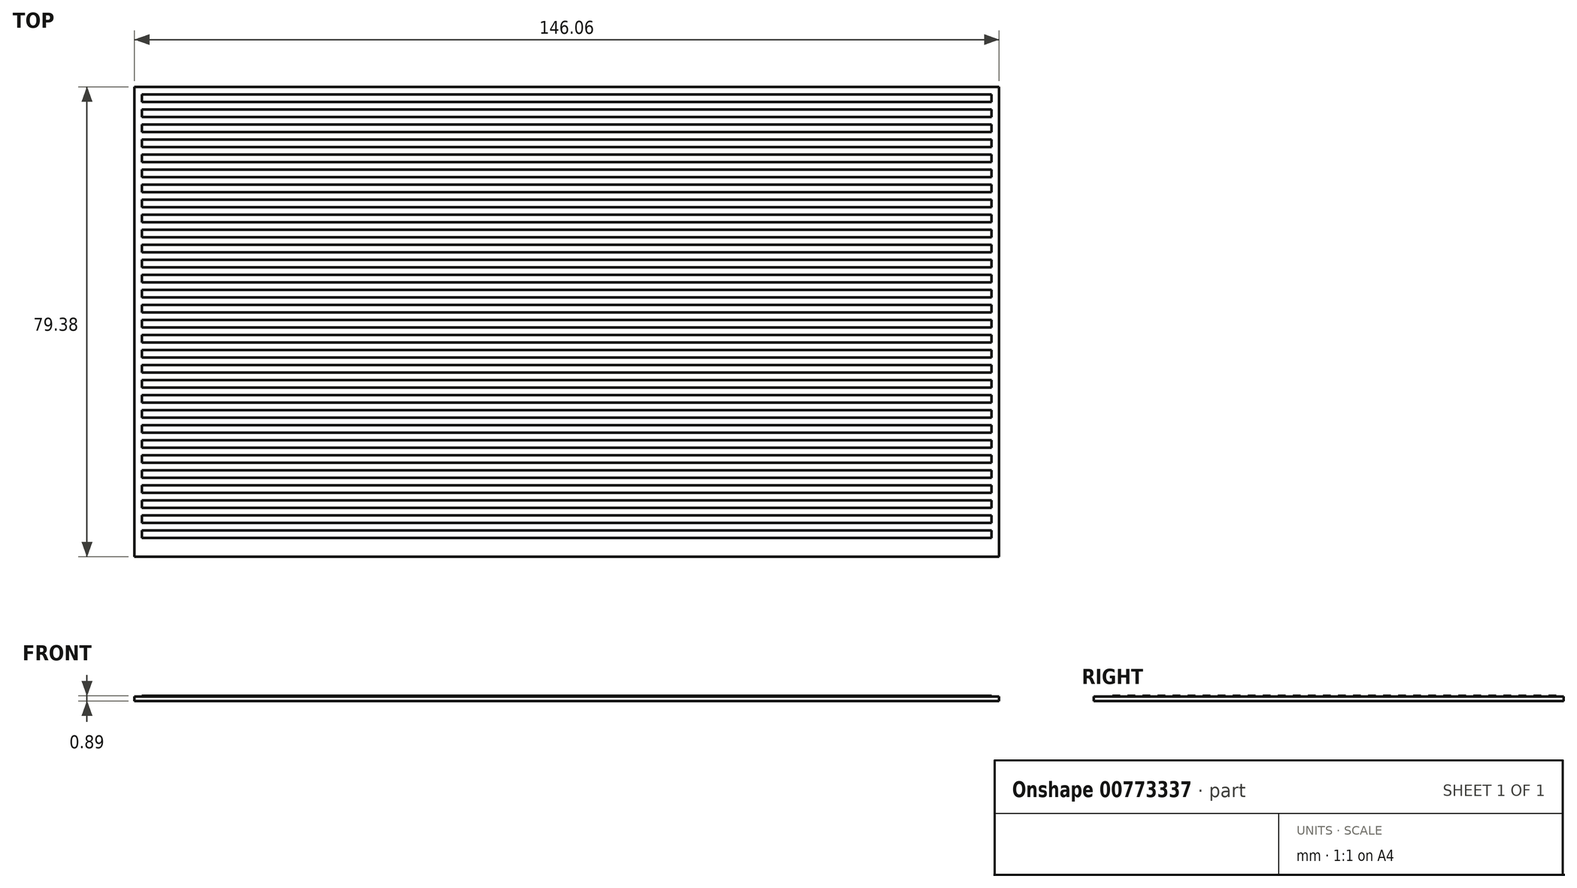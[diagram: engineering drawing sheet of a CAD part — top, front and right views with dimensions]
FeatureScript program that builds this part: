
annotation { "Feature Type Name" : "Feature", "Feature Type Description" : "" }
export const myFeature = defineFeature(function(context is Context, id is Id, definition is map)
    precondition{}
    {
        {
            var Q0;
            Q0=qCreatedBy(makeId("Top.planeOp"),FACE);
            var sketch = newSketch(context, id + "F0", { "sketchPlane" : qUnion([Q0])});
            skLineSegment(sketch, "E0.bottom", {"start": v(73.03, 39.69) * mm, "end": v(-73.03, 39.69) * mm});
            skLineSegment(sketch, "E0.top", {"start": v(73.03, -39.69) * mm, "end": v(-73.03, -39.69) * mm});
            skLineSegment(sketch, "E0.left", {"start": v(73.03, 39.69) * mm, "end": v(73.03, -39.69) * mm});
            skLineSegment(sketch, "E0.right", {"start": v(-73.03, 39.69) * mm, "end": v(-73.03, -39.69) * mm});
            skPoint(sketch, "E0.middle", {"position": v(0, 0) * mm});
            skSolve(sketch);
        }
        {
            var Q0;
            Q0 = qSketchRegion(id + "F0", true);
            extrude(context, id + "F1", {"entities" : qUnion([Q0]), "depth" : 0.76 * mm, "offsetDistance" : 25.4 * mm});
        }
        {
            var Q0;
            Q0=makeQuery(id+"F1.opExtrude","CAP_FACE",FACE,{"disambiguationData":[OSD([sQuery(id+"F0.wireOp",EDGE,"E0.bottom"),sQuery(id+"F0.wireOp",EDGE,"E0.top"),sQuery(id+"F0.wireOp",EDGE,"E0.left"),sQuery(id+"F0.wireOp",EDGE,"E0.right")])],"isStart":false});
            var sketch = newSketch(context, id + "F2", { "sketchPlane" : qUnion([Q0])});
            skLineSegment(sketch, "E1.bottom", {"start": v(-71.76, 38.42) * mm, "end": v(71.76, 38.42) * mm});
            skLineSegment(sketch, "E1.top", {"start": v(-71.76, 37.15) * mm, "end": v(71.76, 37.15) * mm});
            skLineSegment(sketch, "E1.left", {"start": v(-71.76, 38.42) * mm, "end": v(-71.76, 37.15) * mm});
            skLineSegment(sketch, "E1.right", {"start": v(71.76, 38.42) * mm, "end": v(71.76, 37.15) * mm});
            skLineSegment(sketch, "E2.0.1.0", {"start": v(-71.76, 35.88) * mm, "end": v(71.76, 35.88) * mm});
            skLineSegment(sketch, "E2.0.2.0", {"start": v(-71.76, 34.6) * mm, "end": v(71.76, 34.6) * mm});
            skLineSegment(sketch, "E2.0.2.1", {"start": v(-71.76, 35.88) * mm, "end": v(71.76, 35.88) * mm});
            skLineSegment(sketch, "E2.0.2.2", {"start": v(-71.76, 35.88) * mm, "end": v(-71.76, 34.6) * mm});
            skLineSegment(sketch, "E2.0.2.3", {"start": v(71.76, 35.88) * mm, "end": v(71.76, 34.6) * mm});
            skLineSegment(sketch, "E2.0.3.0", {"start": v(-71.76, 33.34) * mm, "end": v(71.76, 33.34) * mm});
            skLineSegment(sketch, "E2.0.3.1", {"start": v(-71.76, 34.6) * mm, "end": v(71.76, 34.6) * mm});
            skLineSegment(sketch, "E2.0.4.0", {"start": v(-71.76, 32.07) * mm, "end": v(71.76, 32.07) * mm});
            skLineSegment(sketch, "E2.0.4.1", {"start": v(-71.76, 33.34) * mm, "end": v(71.76, 33.34) * mm});
            skLineSegment(sketch, "E2.0.4.2", {"start": v(-71.76, 33.34) * mm, "end": v(-71.76, 32.07) * mm});
            skLineSegment(sketch, "E2.0.4.3", {"start": v(71.76, 33.34) * mm, "end": v(71.76, 32.07) * mm});
            skLineSegment(sketch, "E2.0.5.0", {"start": v(-71.76, 30.8) * mm, "end": v(71.76, 30.8) * mm});
            skLineSegment(sketch, "E2.0.5.1", {"start": v(-71.76, 32.07) * mm, "end": v(71.76, 32.07) * mm});
            skLineSegment(sketch, "E2.0.6.0", {"start": v(-71.76, 29.53) * mm, "end": v(71.76, 29.53) * mm});
            skLineSegment(sketch, "E2.0.6.1", {"start": v(-71.76, 30.8) * mm, "end": v(71.76, 30.8) * mm});
            skLineSegment(sketch, "E2.0.6.2", {"start": v(-71.76, 30.8) * mm, "end": v(-71.76, 29.53) * mm});
            skLineSegment(sketch, "E2.0.6.3", {"start": v(71.76, 30.8) * mm, "end": v(71.76, 29.53) * mm});
            skLineSegment(sketch, "E2.0.7.0", {"start": v(-71.76, 28.26) * mm, "end": v(71.76, 28.26) * mm});
            skLineSegment(sketch, "E2.0.7.1", {"start": v(-71.76, 29.53) * mm, "end": v(71.76, 29.53) * mm});
            skLineSegment(sketch, "E2.0.8.0", {"start": v(-71.76, 26.99) * mm, "end": v(71.76, 26.99) * mm});
            skLineSegment(sketch, "E2.0.8.1", {"start": v(-71.76, 28.26) * mm, "end": v(71.76, 28.26) * mm});
            skLineSegment(sketch, "E2.0.8.2", {"start": v(-71.76, 28.26) * mm, "end": v(-71.76, 26.99) * mm});
            skLineSegment(sketch, "E2.0.8.3", {"start": v(71.76, 28.26) * mm, "end": v(71.76, 26.99) * mm});
            skLineSegment(sketch, "E2.0.9.0", {"start": v(-71.76, 25.72) * mm, "end": v(71.76, 25.72) * mm});
            skLineSegment(sketch, "E2.0.9.1", {"start": v(-71.76, 26.99) * mm, "end": v(71.76, 26.99) * mm});
            skLineSegment(sketch, "E2.0.10.0", {"start": v(-71.76, 24.45) * mm, "end": v(71.76, 24.45) * mm});
            skLineSegment(sketch, "E2.0.10.1", {"start": v(-71.76, 25.72) * mm, "end": v(71.76, 25.72) * mm});
            skLineSegment(sketch, "E2.0.10.2", {"start": v(-71.76, 25.72) * mm, "end": v(-71.76, 24.45) * mm});
            skLineSegment(sketch, "E2.0.10.3", {"start": v(71.76, 25.72) * mm, "end": v(71.76, 24.45) * mm});
            skLineSegment(sketch, "E2.0.11.0", {"start": v(-71.76, 23.18) * mm, "end": v(71.76, 23.18) * mm});
            skLineSegment(sketch, "E2.0.11.1", {"start": v(-71.76, 24.45) * mm, "end": v(71.76, 24.45) * mm});
            skLineSegment(sketch, "E2.0.12.0", {"start": v(-71.76, 21.9) * mm, "end": v(71.76, 21.9) * mm});
            skLineSegment(sketch, "E2.0.12.1", {"start": v(-71.76, 23.18) * mm, "end": v(71.76, 23.18) * mm});
            skLineSegment(sketch, "E2.0.12.2", {"start": v(-71.76, 23.18) * mm, "end": v(-71.76, 21.9) * mm});
            skLineSegment(sketch, "E2.0.12.3", {"start": v(71.76, 23.18) * mm, "end": v(71.76, 21.9) * mm});
            skLineSegment(sketch, "E2.0.13.0", {"start": v(-71.76, 20.64) * mm, "end": v(71.76, 20.64) * mm});
            skLineSegment(sketch, "E2.0.13.1", {"start": v(-71.76, 21.9) * mm, "end": v(71.76, 21.9) * mm});
            skLineSegment(sketch, "E2.0.14.0", {"start": v(-71.76, 19.37) * mm, "end": v(71.76, 19.37) * mm});
            skLineSegment(sketch, "E2.0.14.1", {"start": v(-71.76, 20.64) * mm, "end": v(71.76, 20.64) * mm});
            skLineSegment(sketch, "E2.0.14.2", {"start": v(-71.76, 20.64) * mm, "end": v(-71.76, 19.37) * mm});
            skLineSegment(sketch, "E2.0.14.3", {"start": v(71.76, 20.64) * mm, "end": v(71.76, 19.37) * mm});
            skLineSegment(sketch, "E2.0.15.0", {"start": v(-71.76, 18.1) * mm, "end": v(71.76, 18.1) * mm});
            skLineSegment(sketch, "E2.0.15.1", {"start": v(-71.76, 19.37) * mm, "end": v(71.76, 19.37) * mm});
            skLineSegment(sketch, "E2.0.16.0", {"start": v(-71.76, 16.83) * mm, "end": v(71.76, 16.83) * mm});
            skLineSegment(sketch, "E2.0.16.1", {"start": v(-71.76, 18.1) * mm, "end": v(71.76, 18.1) * mm});
            skLineSegment(sketch, "E2.0.16.2", {"start": v(-71.76, 18.1) * mm, "end": v(-71.76, 16.83) * mm});
            skLineSegment(sketch, "E2.0.16.3", {"start": v(71.76, 18.1) * mm, "end": v(71.76, 16.83) * mm});
            skLineSegment(sketch, "E2.0.17.0", {"start": v(-71.76, 15.56) * mm, "end": v(71.76, 15.56) * mm});
            skLineSegment(sketch, "E2.0.17.1", {"start": v(-71.76, 16.83) * mm, "end": v(71.76, 16.83) * mm});
            skLineSegment(sketch, "E2.0.18.0", {"start": v(-71.76, 14.29) * mm, "end": v(71.76, 14.29) * mm});
            skLineSegment(sketch, "E2.0.18.1", {"start": v(-71.76, 15.56) * mm, "end": v(71.76, 15.56) * mm});
            skLineSegment(sketch, "E2.0.18.2", {"start": v(-71.76, 15.56) * mm, "end": v(-71.76, 14.29) * mm});
            skLineSegment(sketch, "E2.0.18.3", {"start": v(71.76, 15.56) * mm, "end": v(71.76, 14.29) * mm});
            skLineSegment(sketch, "E2.0.19.0", {"start": v(-71.76, 13.02) * mm, "end": v(71.76, 13.02) * mm});
            skLineSegment(sketch, "E2.0.19.1", {"start": v(-71.76, 14.29) * mm, "end": v(71.76, 14.29) * mm});
            skLineSegment(sketch, "E2.direction1", {"start": v(-71.76, 37.15) * mm, "end": v(71.76, 37.15) * mm, "construction": true});
            skLineSegment(sketch, "E3.0.0.20", {"start": v(-71.76, 11.75) * mm, "end": v(71.76, 11.75) * mm});
            skLineSegment(sketch, "E3.6.0.20", {"start": v(-71.76, 13.02) * mm, "end": v(-71.76, 11.75) * mm});
            skLineSegment(sketch, "E3.9.0.20", {"start": v(71.76, 13.02) * mm, "end": v(71.76, 11.75) * mm});
            skLineSegment(sketch, "E3.0.0.21", {"start": v(-71.76, 10.48) * mm, "end": v(71.76, 10.48) * mm});
            skLineSegment(sketch, "E3.3.0.21", {"start": v(-71.76, 11.75) * mm, "end": v(71.76, 11.75) * mm});
            skLineSegment(sketch, "E3.0.0.22", {"start": v(-71.76, 9.2) * mm, "end": v(71.76, 9.2) * mm});
            skLineSegment(sketch, "E3.3.0.22", {"start": v(-71.76, 10.48) * mm, "end": v(71.76, 10.48) * mm});
            skLineSegment(sketch, "E3.6.0.22", {"start": v(-71.76, 10.48) * mm, "end": v(-71.76, 9.2) * mm});
            skLineSegment(sketch, "E3.9.0.22", {"start": v(71.76, 10.48) * mm, "end": v(71.76, 9.2) * mm});
            skLineSegment(sketch, "E3.0.0.23", {"start": v(-71.76, 7.94) * mm, "end": v(71.76, 7.94) * mm});
            skLineSegment(sketch, "E3.3.0.23", {"start": v(-71.76, 9.2) * mm, "end": v(71.76, 9.2) * mm});
            skLineSegment(sketch, "E3.0.0.24", {"start": v(-71.76, 6.67) * mm, "end": v(71.76, 6.67) * mm});
            skLineSegment(sketch, "E3.3.0.24", {"start": v(-71.76, 7.94) * mm, "end": v(71.76, 7.94) * mm});
            skLineSegment(sketch, "E3.6.0.24", {"start": v(-71.76, 7.94) * mm, "end": v(-71.76, 6.67) * mm});
            skLineSegment(sketch, "E3.9.0.24", {"start": v(71.76, 7.94) * mm, "end": v(71.76, 6.67) * mm});
            skLineSegment(sketch, "E3.0.0.25", {"start": v(-71.76, 5.4) * mm, "end": v(71.76, 5.4) * mm});
            skLineSegment(sketch, "E3.3.0.25", {"start": v(-71.76, 6.67) * mm, "end": v(71.76, 6.67) * mm});
            skLineSegment(sketch, "E3.0.0.26", {"start": v(-71.76, 4.13) * mm, "end": v(71.76, 4.13) * mm});
            skLineSegment(sketch, "E3.3.0.26", {"start": v(-71.76, 5.4) * mm, "end": v(71.76, 5.4) * mm});
            skLineSegment(sketch, "E3.6.0.26", {"start": v(-71.76, 5.4) * mm, "end": v(-71.76, 4.13) * mm});
            skLineSegment(sketch, "E3.9.0.26", {"start": v(71.76, 5.4) * mm, "end": v(71.76, 4.13) * mm});
            skLineSegment(sketch, "E3.0.0.27", {"start": v(-71.76, 2.86) * mm, "end": v(71.76, 2.86) * mm});
            skLineSegment(sketch, "E3.3.0.27", {"start": v(-71.76, 4.13) * mm, "end": v(71.76, 4.13) * mm});
            skLineSegment(sketch, "E3.0.0.28", {"start": v(-71.76, 1.59) * mm, "end": v(71.76, 1.59) * mm});
            skLineSegment(sketch, "E3.3.0.28", {"start": v(-71.76, 2.86) * mm, "end": v(71.76, 2.86) * mm});
            skLineSegment(sketch, "E3.6.0.28", {"start": v(-71.76, 2.86) * mm, "end": v(-71.76, 1.59) * mm});
            skLineSegment(sketch, "E3.9.0.28", {"start": v(71.76, 2.86) * mm, "end": v(71.76, 1.59) * mm});
            skLineSegment(sketch, "E3.0.0.29", {"start": v(-71.76, 0.32) * mm, "end": v(71.76, 0.32) * mm});
            skLineSegment(sketch, "E3.3.0.29", {"start": v(-71.76, 1.59) * mm, "end": v(71.76, 1.59) * mm});
            skLineSegment(sketch, "E3.0.0.30", {"start": v(-71.76, -0.95) * mm, "end": v(71.76, -0.95) * mm});
            skLineSegment(sketch, "E3.3.0.30", {"start": v(-71.76, 0.32) * mm, "end": v(71.76, 0.32) * mm});
            skLineSegment(sketch, "E3.6.0.30", {"start": v(-71.76, 0.32) * mm, "end": v(-71.76, -0.95) * mm});
            skLineSegment(sketch, "E3.9.0.30", {"start": v(71.76, 0.32) * mm, "end": v(71.76, -0.95) * mm});
            skLineSegment(sketch, "E3.0.0.31", {"start": v(-71.76, -2.22) * mm, "end": v(71.76, -2.22) * mm});
            skLineSegment(sketch, "E3.3.0.31", {"start": v(-71.76, -0.95) * mm, "end": v(71.76, -0.95) * mm});
            skLineSegment(sketch, "E3.0.0.32", {"start": v(-71.76, -3.5) * mm, "end": v(71.76, -3.5) * mm});
            skLineSegment(sketch, "E3.3.0.32", {"start": v(-71.76, -2.22) * mm, "end": v(71.76, -2.22) * mm});
            skLineSegment(sketch, "E3.6.0.32", {"start": v(-71.76, -2.22) * mm, "end": v(-71.76, -3.5) * mm});
            skLineSegment(sketch, "E3.9.0.32", {"start": v(71.76, -2.22) * mm, "end": v(71.76, -3.5) * mm});
            skLineSegment(sketch, "E3.0.0.33", {"start": v(-71.76, -4.76) * mm, "end": v(71.76, -4.76) * mm});
            skLineSegment(sketch, "E3.3.0.33", {"start": v(-71.76, -3.5) * mm, "end": v(71.76, -3.5) * mm});
            skLineSegment(sketch, "E3.0.0.34", {"start": v(-71.76, -6.03) * mm, "end": v(71.76, -6.03) * mm});
            skLineSegment(sketch, "E3.3.0.34", {"start": v(-71.76, -4.76) * mm, "end": v(71.76, -4.76) * mm});
            skLineSegment(sketch, "E3.6.0.34", {"start": v(-71.76, -4.76) * mm, "end": v(-71.76, -6.03) * mm});
            skLineSegment(sketch, "E3.9.0.34", {"start": v(71.76, -4.76) * mm, "end": v(71.76, -6.03) * mm});
            skLineSegment(sketch, "E3.0.0.35", {"start": v(-71.76, -7.3) * mm, "end": v(71.76, -7.3) * mm});
            skLineSegment(sketch, "E3.3.0.35", {"start": v(-71.76, -6.03) * mm, "end": v(71.76, -6.03) * mm});
            skLineSegment(sketch, "E3.0.0.36", {"start": v(-71.76, -8.57) * mm, "end": v(71.76, -8.57) * mm});
            skLineSegment(sketch, "E3.3.0.36", {"start": v(-71.76, -7.3) * mm, "end": v(71.76, -7.3) * mm});
            skLineSegment(sketch, "E3.6.0.36", {"start": v(-71.76, -7.3) * mm, "end": v(-71.76, -8.57) * mm});
            skLineSegment(sketch, "E3.9.0.36", {"start": v(71.76, -7.3) * mm, "end": v(71.76, -8.57) * mm});
            skLineSegment(sketch, "E3.0.0.37", {"start": v(-71.76, -9.84) * mm, "end": v(71.76, -9.84) * mm});
            skLineSegment(sketch, "E3.3.0.37", {"start": v(-71.76, -8.57) * mm, "end": v(71.76, -8.57) * mm});
            skLineSegment(sketch, "E3.0.0.38", {"start": v(-71.76, -11.11) * mm, "end": v(71.76, -11.11) * mm});
            skLineSegment(sketch, "E3.3.0.38", {"start": v(-71.76, -9.84) * mm, "end": v(71.76, -9.84) * mm});
            skLineSegment(sketch, "E3.6.0.38", {"start": v(-71.76, -9.84) * mm, "end": v(-71.76, -11.11) * mm});
            skLineSegment(sketch, "E3.9.0.38", {"start": v(71.76, -9.84) * mm, "end": v(71.76, -11.11) * mm});
            skLineSegment(sketch, "E3.0.0.39", {"start": v(-71.76, -12.38) * mm, "end": v(71.76, -12.38) * mm});
            skLineSegment(sketch, "E3.3.0.39", {"start": v(-71.76, -11.11) * mm, "end": v(71.76, -11.11) * mm});
            skLineSegment(sketch, "E3.0.0.40", {"start": v(-71.76, -13.65) * mm, "end": v(71.76, -13.65) * mm});
            skLineSegment(sketch, "E3.3.0.40", {"start": v(-71.76, -12.38) * mm, "end": v(71.76, -12.38) * mm});
            skLineSegment(sketch, "E3.6.0.40", {"start": v(-71.76, -12.38) * mm, "end": v(-71.76, -13.65) * mm});
            skLineSegment(sketch, "E3.9.0.40", {"start": v(71.76, -12.38) * mm, "end": v(71.76, -13.65) * mm});
            skLineSegment(sketch, "E3.0.0.41", {"start": v(-71.76, -14.92) * mm, "end": v(71.76, -14.92) * mm});
            skLineSegment(sketch, "E3.3.0.41", {"start": v(-71.76, -13.65) * mm, "end": v(71.76, -13.65) * mm});
            skLineSegment(sketch, "E3.0.0.42", {"start": v(-71.76, -16.2) * mm, "end": v(71.76, -16.2) * mm});
            skLineSegment(sketch, "E3.3.0.42", {"start": v(-71.76, -14.92) * mm, "end": v(71.76, -14.92) * mm});
            skLineSegment(sketch, "E3.6.0.42", {"start": v(-71.76, -14.92) * mm, "end": v(-71.76, -16.2) * mm});
            skLineSegment(sketch, "E3.9.0.42", {"start": v(71.76, -14.92) * mm, "end": v(71.76, -16.2) * mm});
            skLineSegment(sketch, "E3.0.0.43", {"start": v(-71.76, -17.46) * mm, "end": v(71.76, -17.46) * mm});
            skLineSegment(sketch, "E3.3.0.43", {"start": v(-71.76, -16.2) * mm, "end": v(71.76, -16.2) * mm});
            skLineSegment(sketch, "E3.0.0.44", {"start": v(-71.76, -18.73) * mm, "end": v(71.76, -18.73) * mm});
            skLineSegment(sketch, "E3.3.0.44", {"start": v(-71.76, -17.46) * mm, "end": v(71.76, -17.46) * mm});
            skLineSegment(sketch, "E3.6.0.44", {"start": v(-71.76, -17.46) * mm, "end": v(-71.76, -18.73) * mm});
            skLineSegment(sketch, "E3.9.0.44", {"start": v(71.76, -17.46) * mm, "end": v(71.76, -18.73) * mm});
            skLineSegment(sketch, "E3.0.0.45", {"start": v(-71.76, -20) * mm, "end": v(71.76, -20) * mm});
            skLineSegment(sketch, "E3.3.0.45", {"start": v(-71.76, -18.73) * mm, "end": v(71.76, -18.73) * mm});
            skLineSegment(sketch, "E3.0.0.46", {"start": v(-71.76, -21.27) * mm, "end": v(71.76, -21.27) * mm});
            skLineSegment(sketch, "E3.3.0.46", {"start": v(-71.76, -20) * mm, "end": v(71.76, -20) * mm});
            skLineSegment(sketch, "E3.6.0.46", {"start": v(-71.76, -20) * mm, "end": v(-71.76, -21.27) * mm});
            skLineSegment(sketch, "E3.9.0.46", {"start": v(71.76, -20) * mm, "end": v(71.76, -21.27) * mm});
            skLineSegment(sketch, "E3.0.0.47", {"start": v(-71.76, -22.54) * mm, "end": v(71.76, -22.54) * mm});
            skLineSegment(sketch, "E3.3.0.47", {"start": v(-71.76, -21.27) * mm, "end": v(71.76, -21.27) * mm});
            skLineSegment(sketch, "E3.0.0.48", {"start": v(-71.76, -23.81) * mm, "end": v(71.76, -23.81) * mm});
            skLineSegment(sketch, "E3.3.0.48", {"start": v(-71.76, -22.54) * mm, "end": v(71.76, -22.54) * mm});
            skLineSegment(sketch, "E3.6.0.48", {"start": v(-71.76, -22.54) * mm, "end": v(-71.76, -23.81) * mm});
            skLineSegment(sketch, "E3.9.0.48", {"start": v(71.76, -22.54) * mm, "end": v(71.76, -23.81) * mm});
            skLineSegment(sketch, "E3.0.0.49", {"start": v(-71.76, -25.08) * mm, "end": v(71.76, -25.08) * mm});
            skLineSegment(sketch, "E3.3.0.49", {"start": v(-71.76, -23.81) * mm, "end": v(71.76, -23.81) * mm});
            skLineSegment(sketch, "E3.0.0.50", {"start": v(-71.76, -26.35) * mm, "end": v(71.76, -26.35) * mm});
            skLineSegment(sketch, "E3.3.0.50", {"start": v(-71.76, -25.08) * mm, "end": v(71.76, -25.08) * mm});
            skLineSegment(sketch, "E3.6.0.50", {"start": v(-71.76, -25.08) * mm, "end": v(-71.76, -26.35) * mm});
            skLineSegment(sketch, "E3.9.0.50", {"start": v(71.76, -25.08) * mm, "end": v(71.76, -26.35) * mm});
            skLineSegment(sketch, "E3.0.0.51", {"start": v(-71.76, -27.62) * mm, "end": v(71.76, -27.62) * mm});
            skLineSegment(sketch, "E3.3.0.51", {"start": v(-71.76, -26.35) * mm, "end": v(71.76, -26.35) * mm});
            skLineSegment(sketch, "E3.0.0.52", {"start": v(-71.76, -28.9) * mm, "end": v(71.76, -28.9) * mm});
            skLineSegment(sketch, "E3.3.0.52", {"start": v(-71.76, -27.62) * mm, "end": v(71.76, -27.62) * mm});
            skLineSegment(sketch, "E3.6.0.52", {"start": v(-71.76, -27.62) * mm, "end": v(-71.76, -28.9) * mm});
            skLineSegment(sketch, "E3.9.0.52", {"start": v(71.76, -27.62) * mm, "end": v(71.76, -28.9) * mm});
            skLineSegment(sketch, "E3.0.0.53", {"start": v(-71.76, -30.16) * mm, "end": v(71.76, -30.16) * mm});
            skLineSegment(sketch, "E3.3.0.53", {"start": v(-71.76, -28.9) * mm, "end": v(71.76, -28.9) * mm});
            skLineSegment(sketch, "E3.0.0.54", {"start": v(-71.76, -31.43) * mm, "end": v(71.76, -31.43) * mm});
            skLineSegment(sketch, "E3.3.0.54", {"start": v(-71.76, -30.16) * mm, "end": v(71.76, -30.16) * mm});
            skLineSegment(sketch, "E3.6.0.54", {"start": v(-71.76, -30.16) * mm, "end": v(-71.76, -31.43) * mm});
            skLineSegment(sketch, "E3.9.0.54", {"start": v(71.76, -30.16) * mm, "end": v(71.76, -31.43) * mm});
            skLineSegment(sketch, "E3.0.0.55", {"start": v(-71.76, -32.7) * mm, "end": v(71.76, -32.7) * mm});
            skLineSegment(sketch, "E3.3.0.55", {"start": v(-71.76, -31.43) * mm, "end": v(71.76, -31.43) * mm});
            skLineSegment(sketch, "E3.0.0.56", {"start": v(-71.76, -33.97) * mm, "end": v(71.76, -33.97) * mm});
            skLineSegment(sketch, "E3.3.0.56", {"start": v(-71.76, -32.7) * mm, "end": v(71.76, -32.7) * mm});
            skLineSegment(sketch, "E3.6.0.56", {"start": v(-71.76, -32.7) * mm, "end": v(-71.76, -33.97) * mm});
            skLineSegment(sketch, "E3.9.0.56", {"start": v(71.76, -32.7) * mm, "end": v(71.76, -33.97) * mm});
            skLineSegment(sketch, "E3.0.0.57", {"start": v(-71.76, -35.24) * mm, "end": v(71.76, -35.24) * mm});
            skLineSegment(sketch, "E3.3.0.57", {"start": v(-71.76, -33.97) * mm, "end": v(71.76, -33.97) * mm});
            skLineSegment(sketch, "E3.0.0.58", {"start": v(-71.76, -36.51) * mm, "end": v(71.76, -36.51) * mm});
            skLineSegment(sketch, "E3.3.0.58", {"start": v(-71.76, -35.24) * mm, "end": v(71.76, -35.24) * mm});
            skLineSegment(sketch, "E3.6.0.58", {"start": v(-71.76, -35.24) * mm, "end": v(-71.76, -36.51) * mm});
            skLineSegment(sketch, "E3.9.0.58", {"start": v(71.76, -35.24) * mm, "end": v(71.76, -36.51) * mm});
            skLineSegment(sketch, "E3.3.0.59", {"start": v(-71.76, -36.51) * mm, "end": v(71.76, -36.51) * mm});
            skSolve(sketch);
        }
        {
            var Q0;
            Q0 = qSketchRegion(id + "F2", true);
            extrude(context, id + "F3", {"entities" : qUnion([Q0]), "operationType" : NewBodyOperationType.ADD, "depth" : 0.13 * mm, "offsetDistance" : 25.4 * mm});
        }
    });
